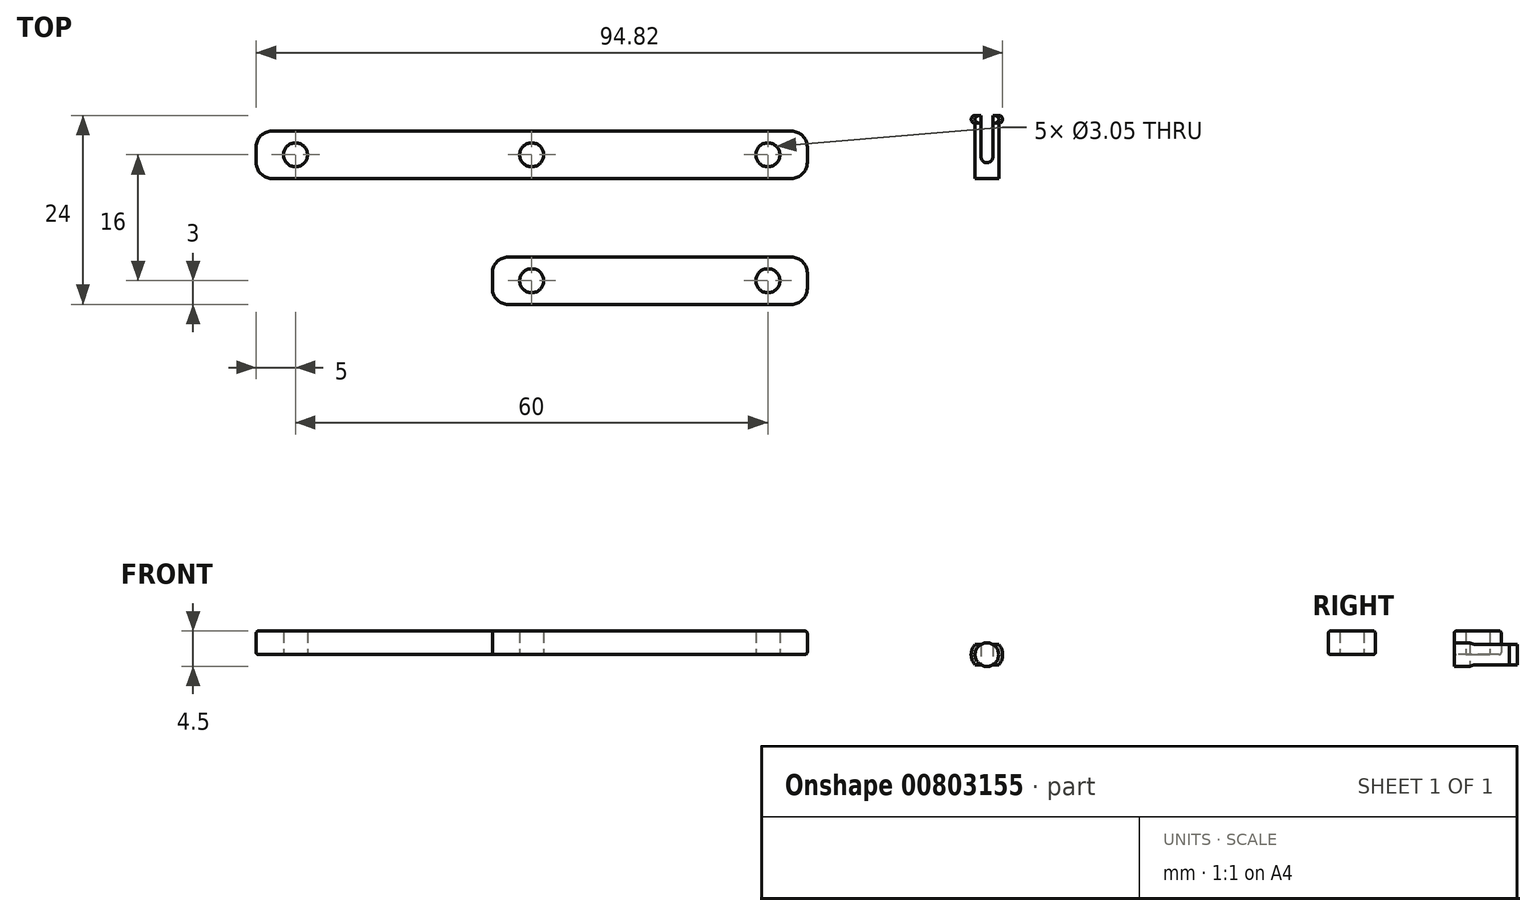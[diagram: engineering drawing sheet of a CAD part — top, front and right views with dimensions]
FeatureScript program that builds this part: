
annotation { "Feature Type Name" : "Feature", "Feature Type Description" : "" }
export const myFeature = defineFeature(function(context is Context, id is Id, definition is map)
    precondition{}
    {
        {
            var Q0;
            Q0=qCreatedBy(makeId("Top.planeOp"),FACE);
            var sketch = newSketch(context, id + "F0", { "sketchPlane" : qUnion([Q0])});
            skLineSegment(sketch, "E0.bottom", {"start": v(-2, 0) * mm, "end": v(-68, 0) * mm});
            skLineSegment(sketch, "E0.top", {"start": v(-2, 6) * mm, "end": v(-68, 6) * mm});
            skLineSegment(sketch, "E0.left", {"start": v(0, 2) * mm, "end": v(0, 4) * mm});
            skLineSegment(sketch, "E0.right", {"start": v(-70, 2) * mm, "end": v(-70, 4) * mm});
            skPoint(sketch, "E1", {"position": v(-70, 3) * mm});
            skPoint(sketch, "E2", {"position": v(-65, 3) * mm});
            skPoint(sketch, "E3", {"position": v(-5, 3) * mm});
            skPoint(sketch, "E4", {"position": v(-35, 3) * mm});
            skCircle(sketch, "E5", {"center": v(-65, 3) * mm, "radius": 1.52 * mm});
            skCircle(sketch, "E6", {"center": v(-35, 3) * mm, "radius": 1.52 * mm});
            skCircle(sketch, "E7", {"center": v(-5, 3) * mm, "radius": 1.52 * mm});
            skPoint(sketch, "E8.visualSharp", {"position": v(-70, 6) * mm});
            skArc(sketch, "E8.filletArc", {"start": v(-68, 6) * mm, "mid": v(-69.41, 5.41) * mm, "end": v(-70, 4) * mm});
            skPoint(sketch, "E9.visualSharp", {"position": v(-70, 0) * mm});
            skArc(sketch, "E9.filletArc", {"start": v(-70, 2) * mm, "mid": v(-69.41, 0.59) * mm, "end": v(-68, 0) * mm});
            skPoint(sketch, "E10.visualSharp", {"position": v(0, 0) * mm});
            skArc(sketch, "E10.filletArc", {"start": v(-2, 0) * mm, "mid": v(-0.59, 0.59) * mm, "end": v(0, 2) * mm});
            skPoint(sketch, "E11.visualSharp", {"position": v(0, 6) * mm});
            skArc(sketch, "E11.filletArc", {"start": v(0, 4) * mm, "mid": v(-0.59, 5.41) * mm, "end": v(-2, 6) * mm});
            skSolve(sketch);
        }
        {
            var Q0;
            Q0=makeQuery(id+"F0.imprint","IMPRINT",FACE,{"disambiguationData":[TD([[makeQuery(id+"F0.imprint","IMPRINT",EDGE,{"derivedFrom":sQuery(id+"F0.wireOp",EDGE,"E0.bottom")}),-1.0]])]});
            extrude(context, id + "F1", {"entities" : qUnion([Q0]), "depth" : 3 * mm, "offsetDistance" : 25 * mm});
        }
        {
            var Q0;
            Q0=qCreatedBy(makeId("Top.planeOp"),FACE);
            var sketch = newSketch(context, id + "F2", { "sketchPlane" : qUnion([Q0])});
            skPoint(sketch, "E12", {"position": v(0, -10) * mm});
            skLineSegment(sketch, "E13.bottom", {"start": v(-2, -10) * mm, "end": v(-38, -10) * mm});
            skLineSegment(sketch, "E13.top", {"start": v(-2, -16) * mm, "end": v(-38, -16) * mm});
            skLineSegment(sketch, "E13.left", {"start": v(0, -12) * mm, "end": v(0, -14) * mm});
            skLineSegment(sketch, "E13.right", {"start": v(-40, -12) * mm, "end": v(-40, -14) * mm});
            skPoint(sketch, "E14", {"position": v(-35, -13) * mm});
            skPoint(sketch, "E14.positionSnap0", {"position": v(-40, -13) * mm});
            skPoint(sketch, "E15", {"position": v(-5, -13) * mm});
            skCircle(sketch, "E16", {"center": v(-35, -13) * mm, "radius": 1.52 * mm});
            skCircle(sketch, "E17", {"center": v(-5, -13) * mm, "radius": 1.52 * mm});
            skPoint(sketch, "E18.visualSharp", {"position": v(-40, -10) * mm});
            skArc(sketch, "E18.filletArc", {"start": v(-38, -10) * mm, "mid": v(-39.41, -10.59) * mm, "end": v(-40, -12) * mm});
            skPoint(sketch, "E19.visualSharp", {"position": v(-40, -16) * mm});
            skArc(sketch, "E19.filletArc", {"start": v(-40, -14) * mm, "mid": v(-39.41, -15.41) * mm, "end": v(-38, -16) * mm});
            skPoint(sketch, "E20.visualSharp", {"position": v(0, -16) * mm});
            skArc(sketch, "E20.filletArc", {"start": v(-2, -16) * mm, "mid": v(-0.59, -15.41) * mm, "end": v(0, -14) * mm});
            skArc(sketch, "E21.filletArc", {"start": v(0, -12) * mm, "mid": v(-0.59, -10.59) * mm, "end": v(-2, -10) * mm});
            skSolve(sketch);
        }
        {
            var Q0;
            Q0=makeQuery(id+"F2.imprint","IMPRINT",FACE,{"disambiguationData":[TD([[makeQuery(id+"F2.imprint","IMPRINT",EDGE,{"derivedFrom":sQuery(id+"F2.wireOp",EDGE,"E13.bottom")}),1.0]])]});
            extrude(context, id + "F3", {"entities" : qUnion([Q0]), "depth" : 3 * mm, "offsetDistance" : 25 * mm});
        }
        {
            var Q0;
            Q0=qCreatedBy(makeId("Top.planeOp"),FACE);
            var sketch = newSketch(context, id + "F4", { "sketchPlane" : qUnion([Q0])});
            skLineSegment(sketch, "E22.bottom", {"start": v(22.82, 0) * mm, "end": v(21.32, 0) * mm});
            skLineSegment(sketch, "E22.top", {"start": v(22.82, 8) * mm, "end": v(21.32, 8) * mm});
            skLineSegment(sketch, "E22.left", {"start": v(22.82, 0) * mm, "end": v(22.82, 8) * mm});
            skLineSegment(sketch, "E22.right", {"start": v(21.32, 0) * mm, "end": v(21.32, 8) * mm});
            skArc(sketch, "E23", {"start": v(21.32, 0) * mm, "mid": v(20.82, 0.5) * mm, "end": v(21.32, 1) * mm});
            skArc(sketch, "E24", {"start": v(21.32, 8) * mm, "mid": v(20.82, 7.5) * mm, "end": v(21.32, 7) * mm});
            skArc(sketch, "E25", {"start": v(22.07, 2.75) * mm, "mid": v(22.82, 2) * mm, "end": v(23.57, 2.75) * mm});
            skLineSegment(sketch, "E26", {"start": v(22.07, 2.75) * mm, "end": v(22.07, 8) * mm});
            skLineSegment(sketch, "E27", {"start": v(23.57, 2.75) * mm, "end": v(23.57, 8) * mm});
            skLineSegment(sketch, "E28", {"start": v(23.57, 8) * mm, "end": v(22.82, 8) * mm});
            skSolve(sketch);
        }
        {
            var Q0;
            {var subQ0=sQuery(id+"F4.wireOp",EDGE,"E24");Q0=makeQuery(id+"F4.imprint","IMPRINT",FACE,{"disambiguationData":[TD([[makeQuery(id+"F4.imprint","IMPRINT",EDGE,{"derivedFrom":subQ0}),1.0]])]});}
            var Q1;
            {var subQ1=sQuery(id+"F4.wireOp",EDGE,"E22.bottom");Q1=makeQuery(id+"F4.imprint","IMPRINT",FACE,{"disambiguationData":[TD([[makeQuery(id+"F4.imprint","IMPRINT",EDGE,{"derivedFrom":subQ1}),-1.0]])]});}
            var Q2;
            {var subQ0=sQuery(id+"F4.wireOp",EDGE,"E23");Q2=makeQuery(id+"F4.imprint","IMPRINT",FACE,{"disambiguationData":[TD([[makeQuery(id+"F4.imprint","IMPRINT",EDGE,{"derivedFrom":subQ0}),-1.0]])]});}
            var Q3;
            {var subQ3=sQuery(id+"F4.wireOp",EDGE,"E26");Q3=makeQuery(id+"F4.imprint","IMPRINT",FACE,{"disambiguationData":[TD([[makeQuery(id+"F4.imprint","IMPRINT",EDGE,{"derivedFrom":subQ3}),-1.0]])]});}
            var Q4;
            Q4=sQuery(id+"F4.wireOp",EDGE,"E22.left");
            revolve(context, id + "F5", {"surfaceOperationType" : NewSurfaceOperationType.NEW, "entities" : qUnion([Q0, Q1, Q2, Q3]), "axis" : qUnion([Q4]), "revolveType" : RevolveType.FULL});
        }
        {
            var Q0;
            {var subQ3=sQuery(id+"F4.wireOp",EDGE,"E26");Q0=makeQuery(id+"F4.imprint","IMPRINT",FACE,{"disambiguationData":[TD([[makeQuery(id+"F4.imprint","IMPRINT",EDGE,{"derivedFrom":subQ3}),-1.0]])]});}
            var Q1;
            {var subQ4=sQuery(id+"F4.wireOp",EDGE,"E27");Q1=makeQuery(id+"F4.imprint","IMPRINT",FACE,{"disambiguationData":[TD([[makeQuery(id+"F4.imprint","IMPRINT",EDGE,{"derivedFrom":subQ4}),1.0]])]});}
            extrude(context, id + "F6", {"entities" : qUnion([Q0, Q1]), "operationType" : NewBodyOperationType.REMOVE, "depth" : 25 * mm, "offsetDistance" : 25 * mm, "hasSecondDirection" : true, "secondDirectionOppositeDirection" : true, "secondDirectionDepth" : 25 * mm});
        }
        {
            var Q0;
            Q0=qCreatedBy(makeId("Right.planeOp"),FACE);
            var sketch = newSketch(context, id + "F7", { "sketchPlane" : qUnion([Q0])});
            skLineSegment(sketch, "E29.bottom", {"start": v(6.58, 1.3) * mm, "end": v(9.32, 1.3) * mm});
            skLineSegment(sketch, "E29.top", {"start": v(6.58, 2.32) * mm, "end": v(9.32, 2.32) * mm});
            skLineSegment(sketch, "E29.left", {"start": v(6.58, 1.3) * mm, "end": v(6.58, 2.32) * mm});
            skLineSegment(sketch, "E29.right", {"start": v(9.32, 1.3) * mm, "end": v(9.32, 2.32) * mm});
            skLineSegment(sketch, "E30.MirrorCS", {"start": v(6.58, -1.3) * mm, "end": v(6.58, -2.32) * mm});
            skLineSegment(sketch, "E31.MirrorCS", {"start": v(6.58, -1.3) * mm, "end": v(9.32, -1.3) * mm});
            skLineSegment(sketch, "E32.MirrorCS", {"start": v(6.58, -2.32) * mm, "end": v(9.32, -2.32) * mm});
            skLineSegment(sketch, "E33.MirrorCS", {"start": v(9.32, -1.3) * mm, "end": v(9.32, -2.32) * mm});
            skSolve(sketch);
        }
        {
            var Q0;
            Q0=makeQuery(id+"F7.imprint","IMPRINT",FACE,{"disambiguationData":[TD([[makeQuery(id+"F7.imprint","IMPRINT",EDGE,{"derivedFrom":sQuery(id+"F7.wireOp",EDGE,"E29.bottom")}),1.0]])]});
            var Q1;
            Q1=makeQuery(id+"F7.imprint","IMPRINT",FACE,{"disambiguationData":[TD([[makeQuery(id+"F7.imprint","IMPRINT",EDGE,{"derivedFrom":sQuery(id+"F7.wireOp",EDGE,"E30.MirrorCS")}),1.0]])]});
            extrude(context, id + "F8", {"entities" : qUnion([Q0, Q1]), "operationType" : NewBodyOperationType.REMOVE, "depth" : 25 * mm, "offsetDistance" : 25 * mm});
        }
        {
            var Q0;
            Q0=makeQuery(id+"F1.opExtrude","CAP_EDGE",EDGE,{"disambiguationData":[OSD([sQuery(id+"F0.wireOp",EDGE,"E0.bottom")])],"isStart":false});
            var Q1;
            Q1=makeQuery(id+"F1.opExtrude","CAP_EDGE",EDGE,{"disambiguationData":[OSD([sQuery(id+"F0.wireOp",EDGE,"E0.top")])],"isStart":false});
            var Q2;
            Q2=makeQuery(id+"F1.opExtrude","CAP_EDGE",EDGE,{"disambiguationData":[OSD([sQuery(id+"F0.wireOp",EDGE,"E8.filletArc")])],"isStart":false});
            var Q3;
            Q3=makeQuery(id+"F1.opExtrude","CAP_EDGE",EDGE,{"disambiguationData":[OSD([sQuery(id+"F0.wireOp",EDGE,"E0.right")])],"isStart":false});
            var Q4;
            Q4=makeQuery(id+"F1.opExtrude","CAP_EDGE",EDGE,{"disambiguationData":[OSD([sQuery(id+"F0.wireOp",EDGE,"E9.filletArc")])],"isStart":false});
            var Q5;
            Q5=makeQuery(id+"F1.opExtrude","CAP_EDGE",EDGE,{"disambiguationData":[OSD([sQuery(id+"F0.wireOp",EDGE,"E9.filletArc")])],"isStart":true});
            var Q6;
            Q6=makeQuery(id+"F1.opExtrude","CAP_EDGE",EDGE,{"disambiguationData":[OSD([sQuery(id+"F0.wireOp",EDGE,"E0.bottom")])],"isStart":true});
            var Q7;
            Q7=makeQuery(id+"F1.opExtrude","CAP_EDGE",EDGE,{"disambiguationData":[OSD([sQuery(id+"F0.wireOp",EDGE,"E0.left")])],"isStart":false});
            var Q8;
            Q8=makeQuery(id+"F1.opExtrude","CAP_EDGE",EDGE,{"disambiguationData":[OSD([sQuery(id+"F0.wireOp",EDGE,"E10.filletArc")])],"isStart":false});
            var Q9;
            Q9=makeQuery(id+"F3.opExtrude","CAP_EDGE",EDGE,{"disambiguationData":[OSD([sQuery(id+"F2.wireOp",EDGE,"E13.bottom")])],"isStart":false});
            var Q10;
            Q10=makeQuery(id+"F3.opExtrude","CAP_EDGE",EDGE,{"disambiguationData":[OSD([sQuery(id+"F2.wireOp",EDGE,"E21.filletArc")])],"isStart":false});
            var Q11;
            Q11=makeQuery(id+"F3.opExtrude","CAP_EDGE",EDGE,{"disambiguationData":[OSD([sQuery(id+"F2.wireOp",EDGE,"E13.left")])],"isStart":false});
            var Q12;
            Q12=makeQuery(id+"F3.opExtrude","CAP_EDGE",EDGE,{"disambiguationData":[OSD([sQuery(id+"F2.wireOp",EDGE,"E20.filletArc")])],"isStart":false});
            var Q13;
            Q13=makeQuery(id+"F3.opExtrude","CAP_EDGE",EDGE,{"disambiguationData":[OSD([sQuery(id+"F2.wireOp",EDGE,"E13.top")])],"isStart":false});
            var Q14;
            Q14=makeQuery(id+"F3.opExtrude","CAP_EDGE",EDGE,{"disambiguationData":[OSD([sQuery(id+"F2.wireOp",EDGE,"E19.filletArc")])],"isStart":false});
            var Q15;
            Q15=makeQuery(id+"F3.opExtrude","CAP_EDGE",EDGE,{"disambiguationData":[OSD([sQuery(id+"F2.wireOp",EDGE,"E13.right")])],"isStart":false});
            var Q16;
            Q16=makeQuery(id+"F3.opExtrude","CAP_EDGE",EDGE,{"disambiguationData":[OSD([sQuery(id+"F2.wireOp",EDGE,"E18.filletArc")])],"isStart":false});
            var Q17;
            Q17=makeQuery(id+"F1.opExtrude","CAP_EDGE",EDGE,{"disambiguationData":[OSD([sQuery(id+"F0.wireOp",EDGE,"E11.filletArc")])],"isStart":false});
            var Q18;
            Q18=makeQuery(id+"F3.opExtrude","CAP_EDGE",EDGE,{"disambiguationData":[OSD([sQuery(id+"F2.wireOp",EDGE,"E13.right")])],"isStart":true});
            var Q19;
            Q19=makeQuery(id+"F3.opExtrude","CAP_EDGE",EDGE,{"disambiguationData":[OSD([sQuery(id+"F2.wireOp",EDGE,"E18.filletArc")])],"isStart":true});
            var Q20;
            Q20=makeQuery(id+"F3.opExtrude","CAP_EDGE",EDGE,{"disambiguationData":[OSD([sQuery(id+"F2.wireOp",EDGE,"E19.filletArc")])],"isStart":true});
            var Q21;
            Q21=makeQuery(id+"F3.opExtrude","CAP_EDGE",EDGE,{"disambiguationData":[OSD([sQuery(id+"F2.wireOp",EDGE,"E13.top")])],"isStart":true});
            var Q22;
            Q22=makeQuery(id+"F3.opExtrude","CAP_EDGE",EDGE,{"disambiguationData":[OSD([sQuery(id+"F2.wireOp",EDGE,"E13.bottom")])],"isStart":true});
            var Q23;
            Q23=makeQuery(id+"F3.opExtrude","CAP_EDGE",EDGE,{"disambiguationData":[OSD([sQuery(id+"F2.wireOp",EDGE,"E20.filletArc")])],"isStart":true});
            var Q24;
            Q24=makeQuery(id+"F3.opExtrude","CAP_EDGE",EDGE,{"disambiguationData":[OSD([sQuery(id+"F2.wireOp",EDGE,"E13.left")])],"isStart":true});
            var Q25;
            Q25=makeQuery(id+"F3.opExtrude","CAP_EDGE",EDGE,{"disambiguationData":[OSD([sQuery(id+"F2.wireOp",EDGE,"E21.filletArc")])],"isStart":true});
            var Q26;
            Q26=makeQuery(id+"F1.opExtrude","CAP_EDGE",EDGE,{"disambiguationData":[OSD([sQuery(id+"F0.wireOp",EDGE,"E0.left")])],"isStart":true});
            var Q27;
            Q27=makeQuery(id+"F1.opExtrude","CAP_EDGE",EDGE,{"disambiguationData":[OSD([sQuery(id+"F0.wireOp",EDGE,"E11.filletArc")])],"isStart":true});
            var Q28;
            Q28=makeQuery(id+"F1.opExtrude","CAP_EDGE",EDGE,{"disambiguationData":[OSD([sQuery(id+"F0.wireOp",EDGE,"E0.top")])],"isStart":true});
            var Q29;
            Q29=makeQuery(id+"F1.opExtrude","CAP_EDGE",EDGE,{"disambiguationData":[OSD([sQuery(id+"F0.wireOp",EDGE,"E8.filletArc")])],"isStart":true});
            var Q30;
            Q30=makeQuery(id+"F1.opExtrude","CAP_EDGE",EDGE,{"disambiguationData":[OSD([sQuery(id+"F0.wireOp",EDGE,"E0.right")])],"isStart":true});
            var Q31;
            Q31=makeQuery(id+"F1.opExtrude","CAP_EDGE",EDGE,{"disambiguationData":[OSD([sQuery(id+"F0.wireOp",EDGE,"E10.filletArc")])],"isStart":true});
            fillet(context, id + "F9", {"entities" : qUnion([Q0, Q1, Q2, Q3, Q4, Q5, Q6, Q7, Q8, Q9, Q10, Q11, Q12, Q13, Q14, Q15, Q16, Q17, Q18, Q19, Q20, Q21, Q22, Q23, Q24, Q25, Q26, Q27, Q28, Q29, Q30, Q31]), "radius" : 0.3 * mm, "tangentPropagation" : true, "allowEdgeOverflow" : false});
        }
    });
